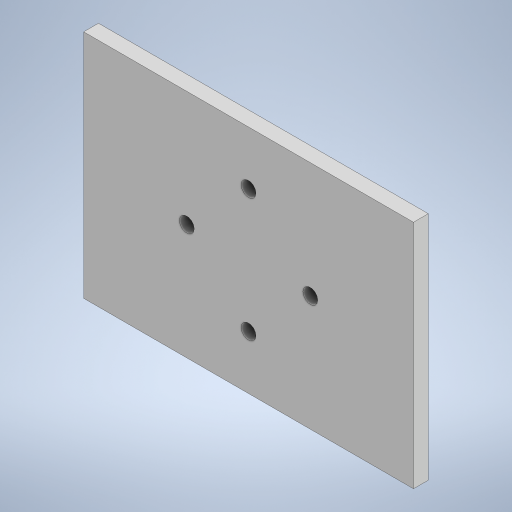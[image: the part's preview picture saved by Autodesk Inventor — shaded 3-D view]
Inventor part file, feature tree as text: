
AUTODESK INVENTOR PART (.ipt)
format: ipt  version: 2024 (Build 280153000, 153)  size: 198,656 bytes
history: native  units: mm
features: extrude x2, sketch x2
ambient origin geometry x8: Origin, YZ Plane, XZ Plane, XY Plane, X Axis, Y Axis, Z Axis, Center Point
bodies: Solid1 (feature_tree)
feature tree (4):
  extrude  "Extrusion1"  Depth=3.0mm TaperAngle=0.0deg
  extrude  "Extrusion2"  [1 undecoded]
  sketch  "Sketch1"  dims[d4=3.0mm d5=0.0mm d16=3.0mm d17=0.0mm]
  sketch  "Sketch2"
note: 1 required parameter value undecoded (feature->parameter linkage not recoverable at this tier; creation-order binding heuristic only, values carry confidence <= 0.55)
